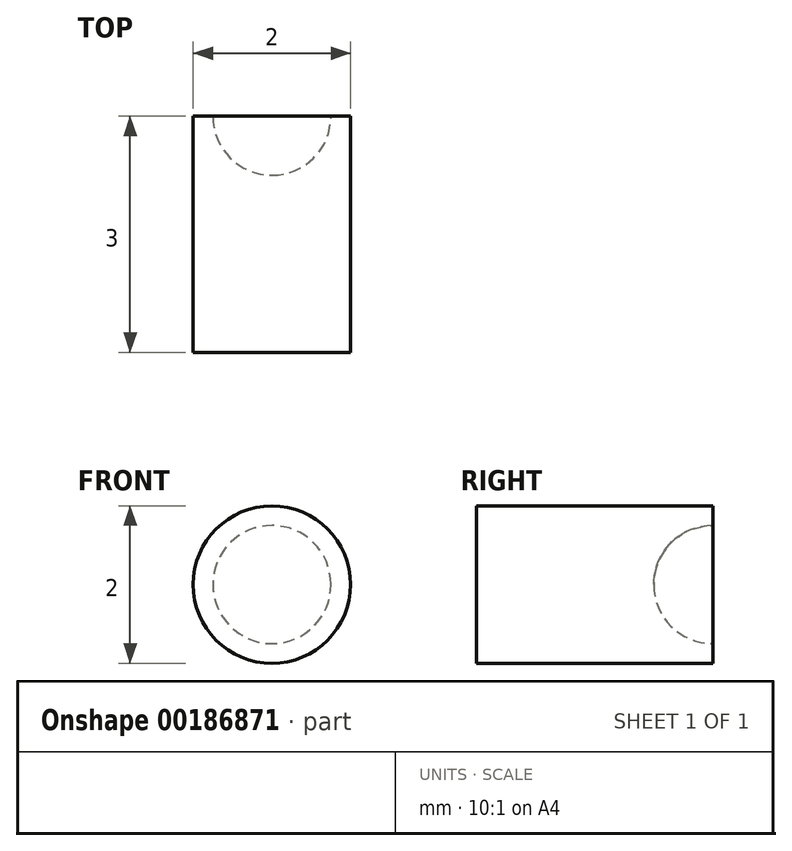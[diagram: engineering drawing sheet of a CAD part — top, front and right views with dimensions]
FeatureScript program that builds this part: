
annotation { "Feature Type Name" : "Feature", "Feature Type Description" : "" }
export const myFeature = defineFeature(function(context is Context, id is Id, definition is map)
    precondition{}
    {
        {
            var Q0;
            Q0=qCreatedBy(makeId("Front.planeOp"),FACE);
            var sketch = newSketch(context, id + "F0", { "sketchPlane" : qUnion([Q0])});
            skCircle(sketch, "E0", {"center": v(0, 0) * mm, "radius": 0.87 * mm});
            skCircle(sketch, "E1", {"center": v(0, 0) * mm, "radius": 1 * mm});
            skSolve(sketch);
        }
        {
            var Q0;
            Q0=makeQuery(id+"F0.imprint","IMPRINT",FACE,{"disambiguationData":[TD([[makeQuery(id+"F0.imprint","IMPRINT",EDGE,{"derivedFrom":sQuery(id+"F0.wireOp",EDGE,"E0")}),-1.0]])]});
            var Q1;
            Q1=makeQuery(id+"F0.imprint","IMPRINT",FACE,{"disambiguationData":[TD([[makeQuery(id+"F0.imprint","IMPRINT",EDGE,{"derivedFrom":sQuery(id+"F0.wireOp",EDGE,"E0")}),1.0]])]});
            var Q2;
            Q2=sQuery(id+"F0.wireOp",EDGE,"E1");
            extrude(context, id + "F1", {"entities" : qUnion([Q0, Q1]), "surfaceEntities" : qUnion([Q2]), "depth" : 3 * mm});
        }
        {
            var Q0;
            Q0=qCreatedBy(makeId("Right.planeOp"),FACE);
            var sketch = newSketch(context, id + "F2", { "sketchPlane" : qUnion([Q0])});
            skArc(sketch, "E2", {"start": v(0, 0.75) * mm, "mid": v(-0.53, 0.53) * mm, "end": v(-0.75, 0) * mm});
            skLineSegment(sketch, "E3", {"start": v(-0.75, 0) * mm, "end": v(0, 0) * mm});
            skLineSegment(sketch, "E4", {"start": v(0, 0) * mm, "end": v(0, 0.75) * mm});
            skSolve(sketch);
        }
        {
            var Q0;
            Q0=makeQuery(id+"F2.imprint","IMPRINT",FACE,{"disambiguationData":[TD([[makeQuery(id+"F2.imprint","IMPRINT",EDGE,{"derivedFrom":sQuery(id+"F2.wireOp",EDGE,"E2")}),1.0]])]});
            var Q1;
            Q1=sQuery(id+"F2.wireOp",EDGE,"E2");
            var Q2;
            Q2=sQuery(id+"F2.wireOp",EDGE,"E3");
            var Q3;
            Q3=sQuery(id+"F2.wireOp",EDGE,"E4");
            var Q4;
            Q4=sQuery(id+"F2.wireOp",EDGE,"E3");
            revolve(context, id + "F3", {"operationType" : NewBodyOperationType.REMOVE, "entities" : qUnion([Q0]), "surfaceEntities" : qUnion([Q1, Q2, Q3]), "axis" : qUnion([Q4]), "revolveType" : RevolveType.FULL, "oppositeDirection" : true});
        }
    });
